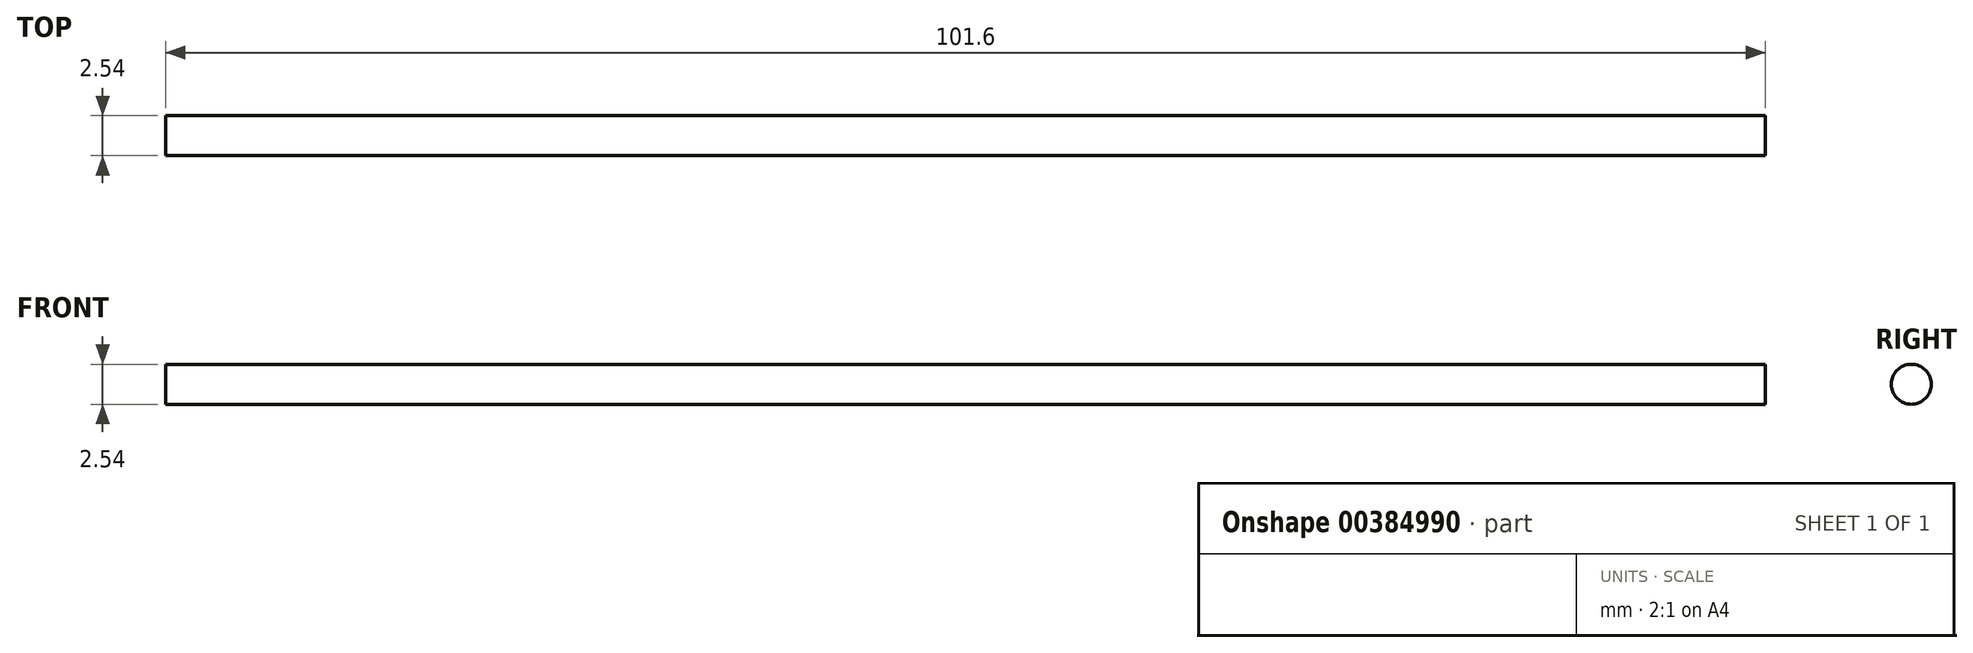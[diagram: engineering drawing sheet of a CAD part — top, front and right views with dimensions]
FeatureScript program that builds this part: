
annotation { "Feature Type Name" : "Feature", "Feature Type Description" : "" }
export const myFeature = defineFeature(function(context is Context, id is Id, definition is map)
    precondition{}
    {
        {
            var Q0;
            Q0=qCreatedBy(makeId("Right.planeOp"),FACE);
            var sketch = newSketch(context, id + "F0", { "sketchPlane" : qUnion([Q0])});
            skCircle(sketch, "E0", {"center": v(-162.56, 0) * mm, "radius": 1.27 * mm});
            skLineSegment(sketch, "E1.bottom", {"start": v(-162.56, 1.27) * mm, "end": v(243.84, 1.27) * mm});
            skLineSegment(sketch, "E1.top", {"start": v(-162.56, -1.27) * mm, "end": v(243.84, -1.27) * mm});
            skLineSegment(sketch, "E1.left", {"start": v(-162.56, 1.27) * mm, "end": v(-162.56, -1.27) * mm});
            skLineSegment(sketch, "E1.right", {"start": v(243.84, 1.27) * mm, "end": v(243.84, -1.27) * mm});
            skSolve(sketch);
        }
        {
            var Q0;
            {var subQ0=sQuery(id+"F0.wireOp",EDGE,"E1.left");Q0=makeQuery(id+"F0.imprint","IMPRINT",FACE,{"disambiguationData":[TD([[makeQuery(id+"F0.imprint","IMPRINT",EDGE,{"derivedFrom":subQ0}),1.0]])]});}
            var Q1;
            {var subQ0=sQuery(id+"F0.wireOp",EDGE,"E1.left");Q1=makeQuery(id+"F0.imprint","IMPRINT",FACE,{"disambiguationData":[TD([[makeQuery(id+"F0.imprint","IMPRINT",EDGE,{"derivedFrom":subQ0}),-1.0]])]});}
            extrude(context, id + "F1", {"entities" : qUnion([Q0, Q1]), "endBound" : BoundingType.SYMMETRIC, "depth" : 101.6 * mm, "offsetDistance" : 25.4 * mm});
        }
    });
